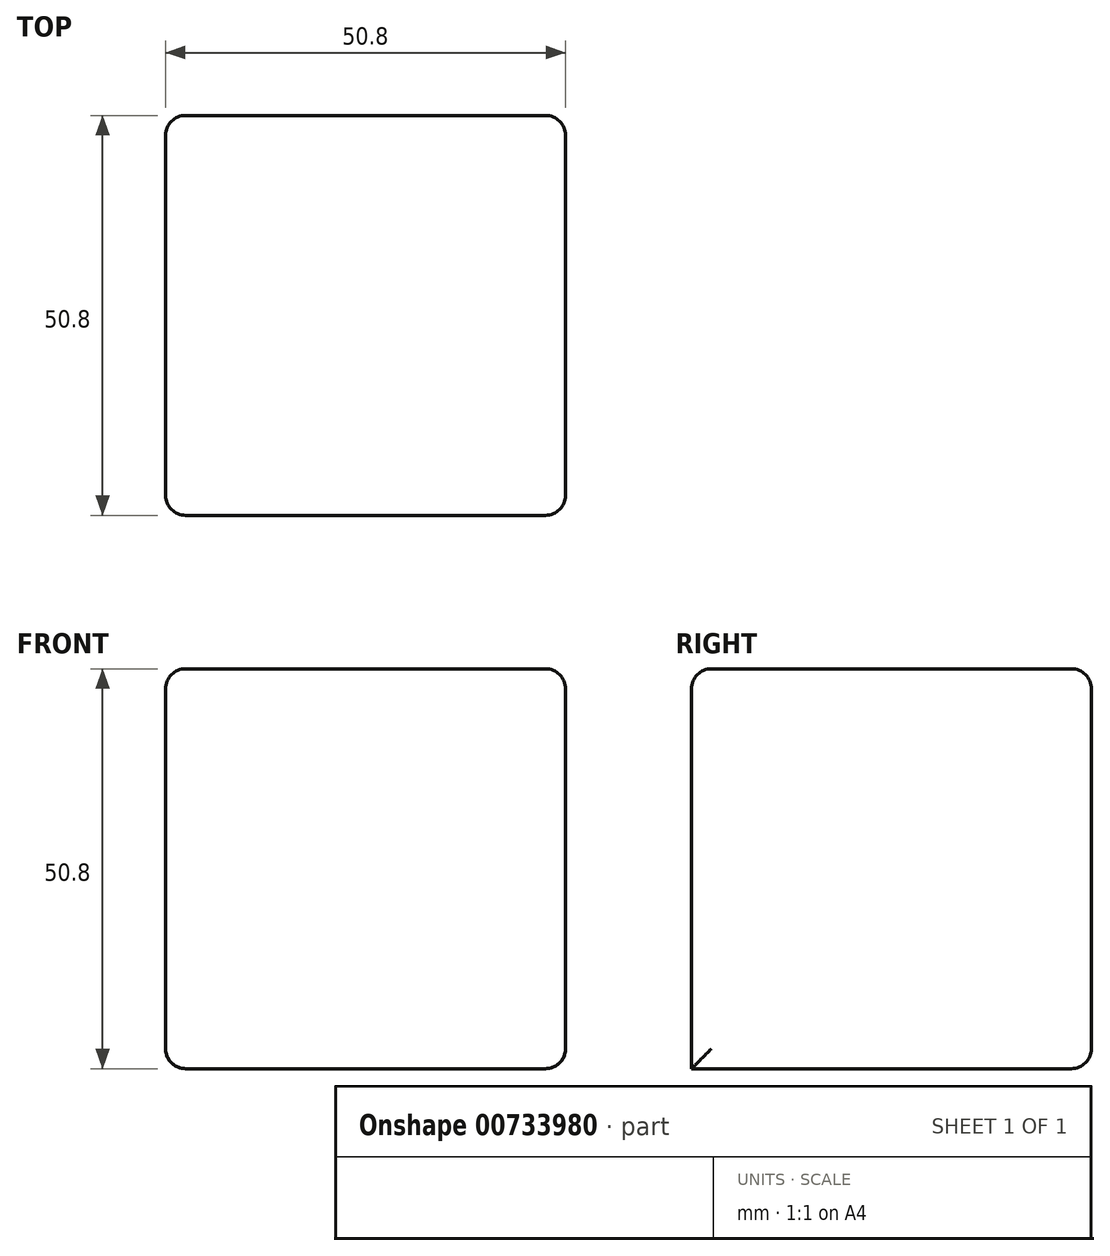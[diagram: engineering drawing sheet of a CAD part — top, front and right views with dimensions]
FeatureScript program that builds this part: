
annotation { "Feature Type Name" : "Feature", "Feature Type Description" : "" }
export const myFeature = defineFeature(function(context is Context, id is Id, definition is map)
    precondition{}
    {
        {
            var Q0;
            Q0=qCreatedBy(makeId("Top.planeOp"),FACE);
            var sketch = newSketch(context, id + "F0", { "sketchPlane" : qUnion([Q0])});
            skLineSegment(sketch, "E0.bottom", {"start": v(635, 395.11) * mm, "end": v(-635, 395.11) * mm});
            skLineSegment(sketch, "E0.top", {"start": v(635, -395.11) * mm, "end": v(-635, -395.11) * mm});
            skLineSegment(sketch, "E0.left", {"start": v(635, 395.11) * mm, "end": v(635, -395.11) * mm});
            skLineSegment(sketch, "E0.right", {"start": v(-635, 395.11) * mm, "end": v(-635, -395.11) * mm});
            skPoint(sketch, "E0.middle", {"position": v(0, 0) * mm});
            skLineSegment(sketch, "E1.bottom", {"start": v(25.4, 25.4) * mm, "end": v(-25.4, 25.4) * mm});
            skLineSegment(sketch, "E1.top", {"start": v(25.4, -25.4) * mm, "end": v(-25.4, -25.4) * mm});
            skLineSegment(sketch, "E1.left", {"start": v(25.4, 25.4) * mm, "end": v(25.4, -25.4) * mm});
            skLineSegment(sketch, "E1.right", {"start": v(-25.4, 25.4) * mm, "end": v(-25.4, -25.4) * mm});
            skSolve(sketch);
        }
        {
            var Q0;
            Q0=makeQuery(id+"F0.imprint","IMPRINT",FACE,{"disambiguationData":[TD([[makeQuery(id+"F0.imprint","IMPRINT",EDGE,{"derivedFrom":sQuery(id+"F0.wireOp",EDGE,"E1.bottom")}),1.0]])]});
            extrude(context, id + "F1", {"entities" : qUnion([Q0]), "depth" : 50.8 * mm, "offsetDistance" : 25.4 * mm});
        }
        {
            var Q0;
            Q0=makeQuery(id+"F1.opExtrude","SWEPT_FACE",FACE,{"disambiguationData":[OSD([sQuery(id+"F0.wireOp",EDGE,"E1.right")])]});
            fillet(context, id + "F2", {"entities" : qUnion([Q0]), "radius" : 2.54 * mm, "tangentPropagation" : true, "allowEdgeOverflow" : false});
        }
        {
            var Q0;
            Q0=makeQuery(id+"F1.opExtrude","CAP_FACE",FACE,{"disambiguationData":[OSD([sQuery(id+"F0.wireOp",EDGE,"E1.bottom"),sQuery(id+"F0.wireOp",EDGE,"E1.top"),sQuery(id+"F0.wireOp",EDGE,"E1.left"),sQuery(id+"F0.wireOp",EDGE,"E1.right")])],"isStart":false});
            var Q1;
            Q1=makeQuery(id+"F1.opExtrude","SWEPT_FACE",FACE,{"disambiguationData":[OSD([sQuery(id+"F0.wireOp",EDGE,"E1.left")])]});
            var Q2;
            Q2=makeQuery(id+"F1.opExtrude","SWEPT_FACE",FACE,{"disambiguationData":[OSD([sQuery(id+"F0.wireOp",EDGE,"E1.bottom")])]});
            fillet(context, id + "F3", {"entities" : qUnion([Q0, Q1, Q2]), "radius" : 2.54 * mm, "tangentPropagation" : true, "allowEdgeOverflow" : false});
        }
    });
